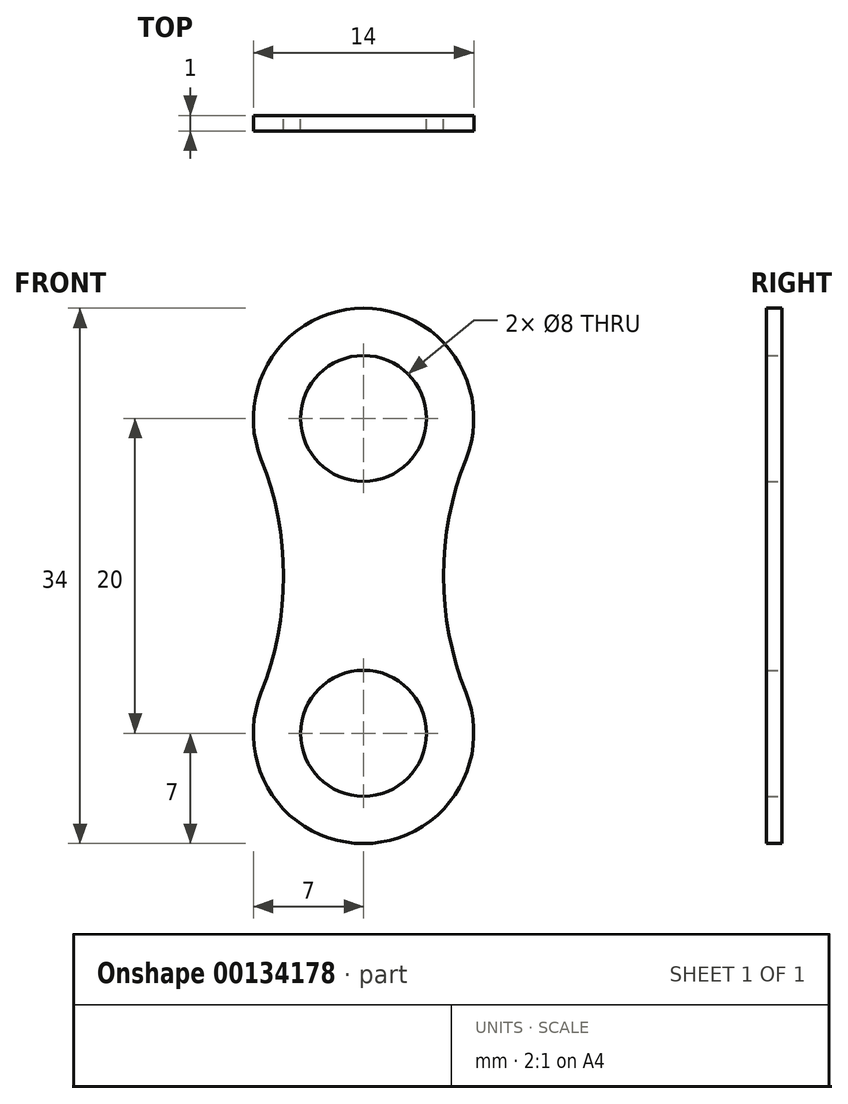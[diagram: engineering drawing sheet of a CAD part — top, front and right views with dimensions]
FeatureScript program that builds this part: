
annotation { "Feature Type Name" : "Feature", "Feature Type Description" : "" }
export const myFeature = defineFeature(function(context is Context, id is Id, definition is map)
    precondition{}
    {
        {
            var Q0;
            Q0=qCreatedBy(makeId("Front.planeOp"),FACE);
            var sketch = newSketch(context, id + "F0", { "sketchPlane" : qUnion([Q0])});
            skArc(sketch, "E0", {"start": v(6.5, 7.4) * mm, "mid": v(0, 17) * mm, "end": v(-6.5, 7.4) * mm});
            skArc(sketch, "E1", {"start": v(-6.5, -7.4) * mm, "mid": v(0, -17) * mm, "end": v(6.5, -7.4) * mm});
            skArc(sketch, "E2", {"start": v(-6.5, -7.4) * mm, "mid": v(-5.08, 0) * mm, "end": v(-6.5, 7.4) * mm});
            skArc(sketch, "E3", {"start": v(6.5, 7.4) * mm, "mid": v(5.08, 0) * mm, "end": v(6.5, -7.4) * mm});
            skCircle(sketch, "E4", {"center": v(0, 10) * mm, "radius": 4 * mm});
            skCircle(sketch, "E5", {"center": v(0, -10) * mm, "radius": 4 * mm});
            skSolve(sketch);
        }
        {
            var Q0;
            Q0=makeQuery(id+"F0.imprint","IMPRINT",FACE,{"disambiguationData":[TD([[makeQuery(id+"F0.imprint","IMPRINT",EDGE,{"derivedFrom":sQuery(id+"F0.wireOp",EDGE,"E0")}),1.0]])]});
            extrude(context, id + "F1", {"entities" : qUnion([Q0]), "depth" : 1 * mm});
        }
    });
